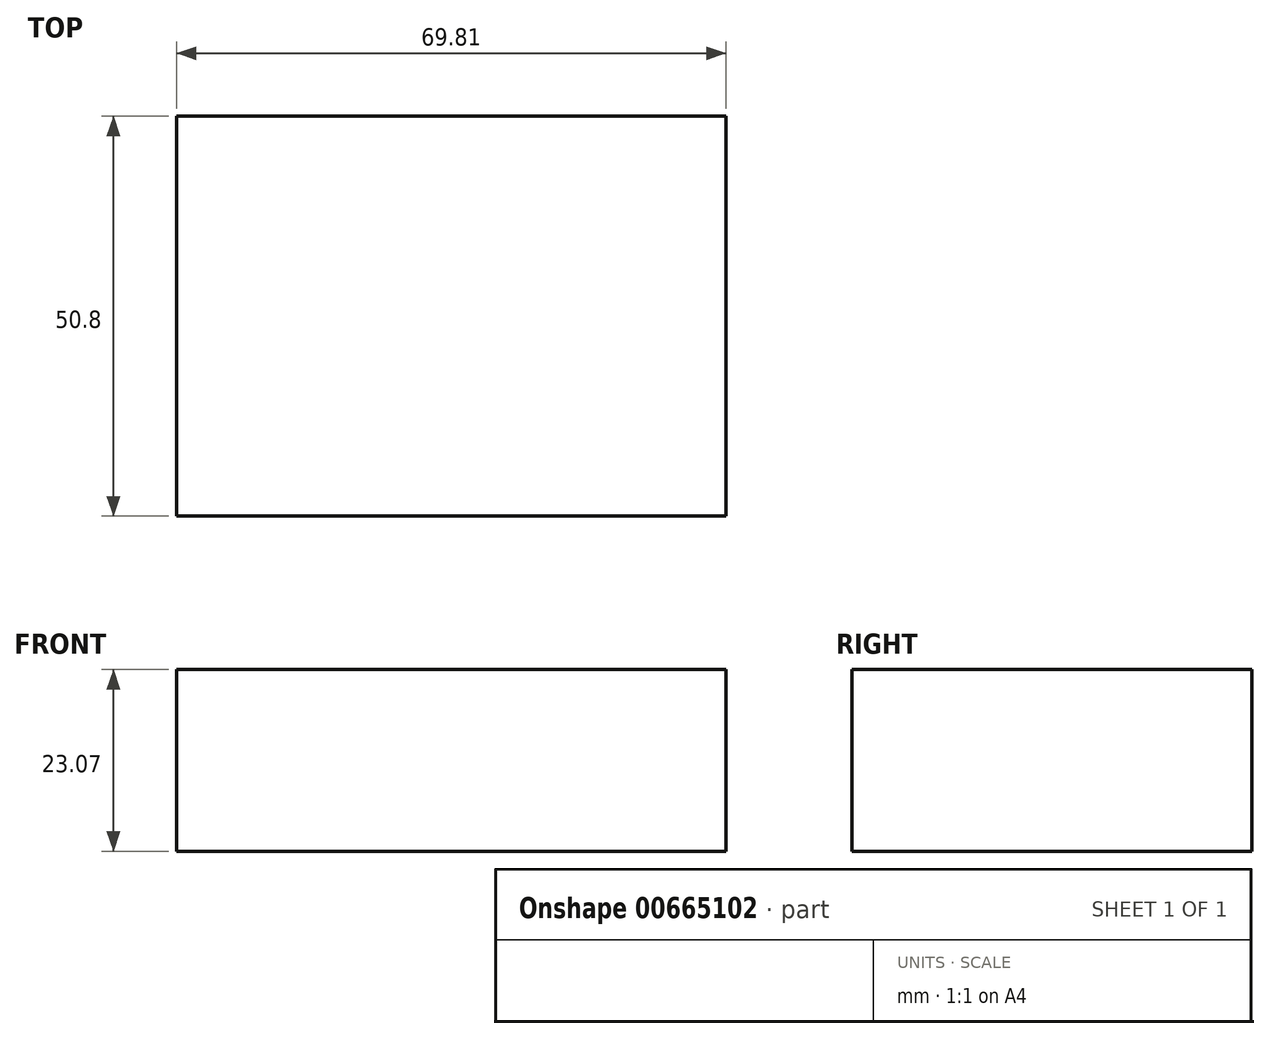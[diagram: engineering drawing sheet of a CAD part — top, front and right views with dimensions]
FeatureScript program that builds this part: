
annotation { "Feature Type Name" : "Feature", "Feature Type Description" : "" }
export const myFeature = defineFeature(function(context is Context, id is Id, definition is map)
    precondition{}
    {
        {
            var Q0;
            Q0=qCreatedBy(makeId("Front.planeOp"),FACE);
            var sketch = newSketch(context, id + "F0", { "sketchPlane" : qUnion([Q0])});
            skLineSegment(sketch, "E0.bottom", {"start": v(0, 0) * mm, "end": v(0, 0) * mm});
            skLineSegment(sketch, "E0.top", {"start": v(0, 0) * mm, "end": v(0, 0) * mm});
            skLineSegment(sketch, "E0.left", {"start": v(0, 0) * mm, "end": v(0, 0) * mm});
            skLineSegment(sketch, "E0.right", {"start": v(0, 0) * mm, "end": v(0, 0) * mm});
            skLineSegment(sketch, "E1.bottom", {"start": v(69.81, 23.07) * mm, "end": v(0, 23.07) * mm});
            skLineSegment(sketch, "E1.top", {"start": v(69.81, 0) * mm, "end": v(0, 0) * mm});
            skLineSegment(sketch, "E1.left", {"start": v(69.81, 23.07) * mm, "end": v(69.81, 0) * mm});
            skLineSegment(sketch, "E1.right", {"start": v(0, 23.07) * mm, "end": v(0, 0) * mm});
            skSolve(sketch);
        }
        {
            var Q0;
            Q0=sQuery(id+"F0.wireOp",EDGE,"E1.top");
            var Q1;
            Q1=sQuery(id+"F0.wireOp",EDGE,"E1.bottom");
            var Q2;
            Q2=sQuery(id+"F0.wireOp",EDGE,"E1.left");
            var Q3;
            Q3=sQuery(id+"F0.wireOp",EDGE,"E1.right");
            extrude(context, id + "F1", {"bodyType" : ToolBodyType.SURFACE, "surfaceEntities" : qUnion([Q0, Q1, Q2, Q3]), "depth" : 25.4 * mm, "offsetDistance" : 25.4 * mm, "hasSecondDirection" : true, "secondDirectionOppositeDirection" : true, "secondDirectionDepth" : 25.4 * mm});
        }
    });
